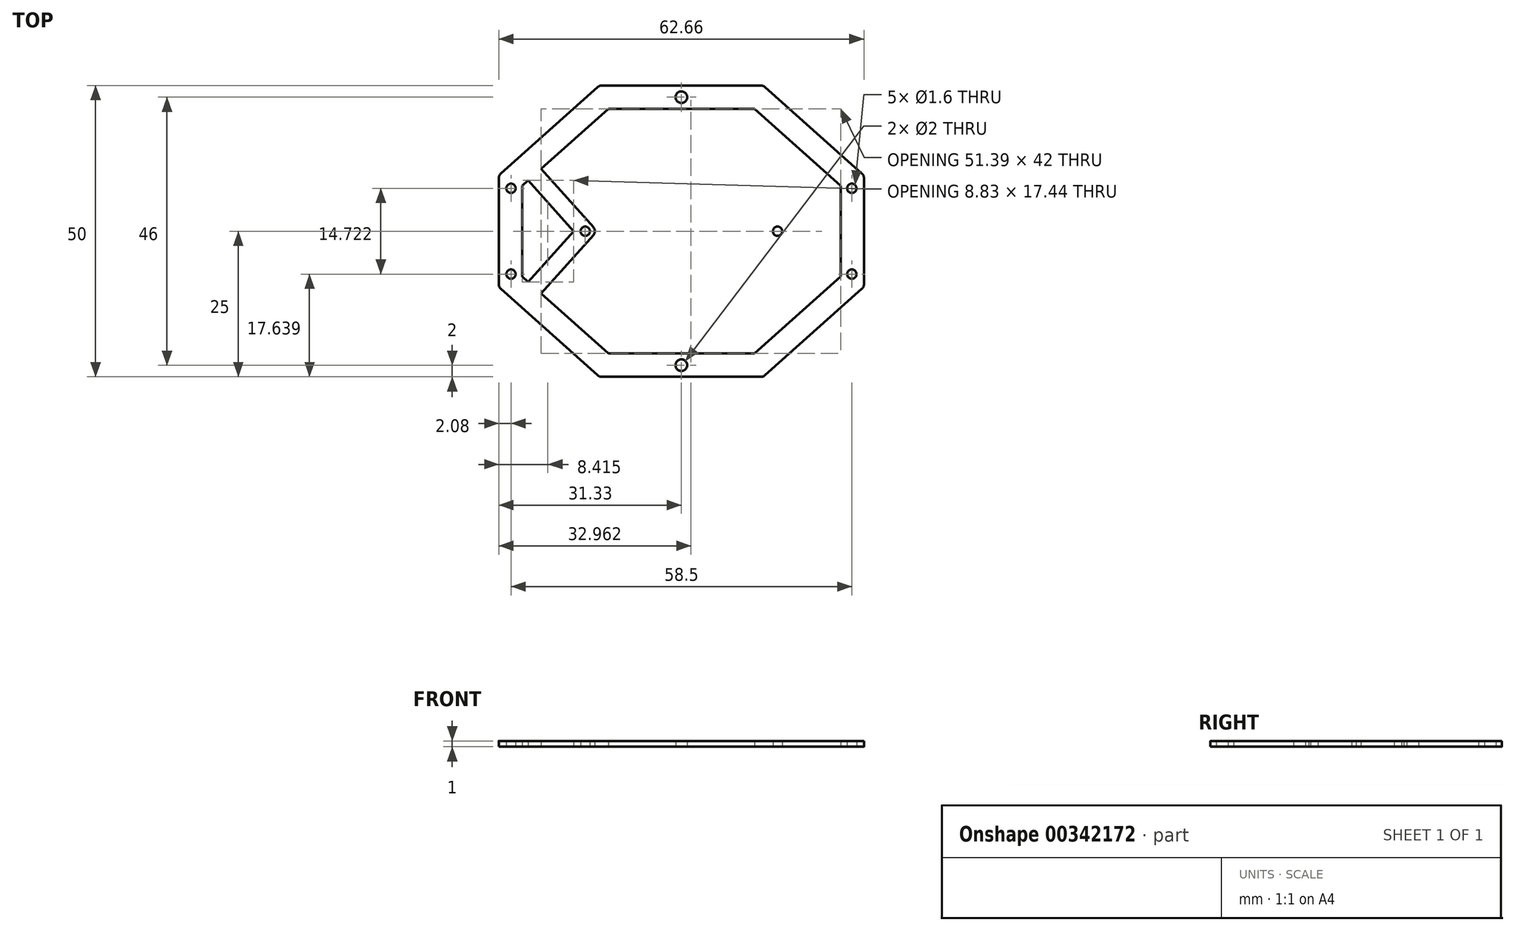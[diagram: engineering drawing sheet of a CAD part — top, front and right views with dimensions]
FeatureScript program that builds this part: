
annotation { "Feature Type Name" : "Feature", "Feature Type Description" : "" }
export const myFeature = defineFeature(function(context is Context, id is Id, definition is map)
    precondition{}
    {
        {
            var Q0;
            Q0=qCreatedBy(makeId("Top.planeOp"),FACE);
            var sketch = newSketch(context, id + "F0", { "sketchPlane" : qUnion([Q0])});
            skPoint(sketch, "E0", {"position": v(0, 25) * mm});
            skPoint(sketch, "E1", {"position": v(25, 0) * mm});
            skPoint(sketch, "E2", {"position": v(16.5, 0) * mm});
            skPoint(sketch, "E3.1.0", {"position": v(29.25, -7.36) * mm});
            skPoint(sketch, "E3.2.0", {"position": v(29.25, 7.36) * mm});
            skLineSegment(sketch, "E4", {"start": v(0, 25) * mm, "end": v(14.07, 25) * mm});
            skPoint(sketch, "E5.MirrorP", {"position": v(-29.25, 7.36) * mm});
            skPoint(sketch, "E6.MirrorP", {"position": v(-16.5, 0) * mm});
            skPoint(sketch, "E7.MirrorP", {"position": v(-25, 0) * mm});
            skPoint(sketch, "E8.MirrorP", {"position": v(-29.25, -7.36) * mm});
            skCircle(sketch, "E9", {"center": v(29.25, 7.36) * mm, "radius": 0.8 * mm});
            skCircle(sketch, "E10.1.0", {"center": v(16.5, 0) * mm, "radius": 0.8 * mm});
            skCircle(sketch, "E10.2.0", {"center": v(29.25, -7.36) * mm, "radius": 0.8 * mm});
            skLineSegment(sketch, "E11", {"start": v(31.33, 0) * mm, "end": v(31.33, 9.58) * mm});
            skLineSegment(sketch, "E12", {"start": v(14.07, 25) * mm, "end": v(31.33, 9.58) * mm});
            skLineSegment(sketch, "E13.0", {"start": v(27.33, -0.08) * mm, "end": v(27.33, 7.8) * mm});
            skLineSegment(sketch, "E13.1", {"start": v(12.54, 21) * mm, "end": v(27.33, 7.8) * mm});
            skLineSegment(sketch, "E13.2", {"start": v(0, 21) * mm, "end": v(12.54, 21) * mm});
            skPoint(sketch, "E14", {"position": v(18.5, 0) * mm});
            skLineSegment(sketch, "E15", {"start": v(18.5, 0) * mm, "end": v(28.95, 11.7) * mm});
            skPoint(sketch, "E16", {"position": v(26.29, 8.72) * mm});
            skPoint(sketch, "E17", {"position": v(14.5, 0) * mm});
            skLineSegment(sketch, "E18", {"start": v(14.5, 0) * mm, "end": v(26.73, 13.69) * mm});
            skPoint(sketch, "E19", {"position": v(24.06, 10.7) * mm});
            skPoint(sketch, "E20", {"position": v(26.73, 13.69) * mm});
            skPoint(sketch, "E21", {"position": v(28.95, 11.7) * mm});
            skCircle(sketch, "E22.MirrorC", {"center": v(-29.25, -7.36) * mm, "radius": 0.8 * mm});
            skCircle(sketch, "E23.MirrorC", {"center": v(-29.25, 7.36) * mm, "radius": 0.8 * mm});
            skCircle(sketch, "E24.MirrorC", {"center": v(-16.5, 0) * mm, "radius": 0.8 * mm});
            skPoint(sketch, "E25.MirrorP", {"position": v(-14.5, 0) * mm});
            skLineSegment(sketch, "E26.MirrorCS", {"start": v(-14.07, 25) * mm, "end": v(-31.33, 9.58) * mm});
            skLineSegment(sketch, "E27.MirrorCS", {"start": v(0, 21) * mm, "end": v(-12.54, 21) * mm});
            skLineSegment(sketch, "E28.MirrorCS", {"start": v(-18.5, 0) * mm, "end": v(-28.95, 11.7) * mm});
            skLineSegment(sketch, "E29.MirrorCS", {"start": v(-31.33, 0) * mm, "end": v(-31.33, 9.58) * mm});
            skPoint(sketch, "E30.MirrorP", {"position": v(-24.06, 10.7) * mm});
            skPoint(sketch, "E31.MirrorP", {"position": v(-26.73, 13.69) * mm});
            skPoint(sketch, "E32.MirrorP", {"position": v(-26.29, 8.72) * mm});
            skLineSegment(sketch, "E33.MirrorCS", {"start": v(-14.5, 0) * mm, "end": v(-26.73, 13.69) * mm});
            skLineSegment(sketch, "E34.MirrorCS", {"start": v(-12.54, 21) * mm, "end": v(-27.33, 7.8) * mm});
            skPoint(sketch, "E35.MirrorP", {"position": v(-18.5, 0) * mm});
            skPoint(sketch, "E36.MirrorP", {"position": v(-28.95, 11.7) * mm});
            skLineSegment(sketch, "E37.MirrorCS", {"start": v(0, 25) * mm, "end": v(-14.07, 25) * mm});
            skLineSegment(sketch, "E38.MirrorCS", {"start": v(-27.33, -0.08) * mm, "end": v(-27.33, 7.8) * mm});
            skPoint(sketch, "E39.MirrorP", {"position": v(0, -25) * mm});
            skLineSegment(sketch, "E40.MirrorCS", {"start": v(-14.5, 0) * mm, "end": v(-26.73, -13.69) * mm});
            skPoint(sketch, "E41.MirrorP", {"position": v(26.73, -13.69) * mm});
            skPoint(sketch, "E42.MirrorP", {"position": v(26.29, -8.72) * mm});
            skPoint(sketch, "E43.MirrorP", {"position": v(-26.29, -8.72) * mm});
            skLineSegment(sketch, "E44.MirrorCS", {"start": v(-31.33, 0) * mm, "end": v(-31.33, -9.58) * mm});
            skLineSegment(sketch, "E45.MirrorCS", {"start": v(-27.33, 0.08) * mm, "end": v(-27.33, -7.8) * mm});
            skPoint(sketch, "E46.MirrorP", {"position": v(24.06, -10.7) * mm});
            skPoint(sketch, "E47.MirrorP", {"position": v(-26.73, -13.69) * mm});
            skLineSegment(sketch, "E48.MirrorCS", {"start": v(-18.5, 0) * mm, "end": v(-28.95, -11.7) * mm});
            skLineSegment(sketch, "E49.MirrorCS", {"start": v(0, -25) * mm, "end": v(-14.07, -25) * mm});
            skLineSegment(sketch, "E50.MirrorCS", {"start": v(14.07, -25) * mm, "end": v(31.33, -9.58) * mm});
            skPoint(sketch, "E51.MirrorP", {"position": v(28.95, -11.7) * mm});
            skLineSegment(sketch, "E52.MirrorCS", {"start": v(31.33, 0) * mm, "end": v(31.33, -9.58) * mm});
            skLineSegment(sketch, "E53.MirrorCS", {"start": v(18.5, 0) * mm, "end": v(28.95, -11.7) * mm});
            skLineSegment(sketch, "E54.MirrorCS", {"start": v(-14.07, -25) * mm, "end": v(-31.33, -9.58) * mm});
            skLineSegment(sketch, "E55.MirrorCS", {"start": v(-12.54, -21) * mm, "end": v(-27.33, -7.8) * mm});
            skLineSegment(sketch, "E56.MirrorCS", {"start": v(14.5, 0) * mm, "end": v(26.73, -13.69) * mm});
            skPoint(sketch, "E57.MirrorP", {"position": v(-24.06, -10.7) * mm});
            skLineSegment(sketch, "E58.MirrorCS", {"start": v(0, -25) * mm, "end": v(14.07, -25) * mm});
            skLineSegment(sketch, "E59.MirrorCS", {"start": v(0, -21) * mm, "end": v(-12.54, -21) * mm});
            skLineSegment(sketch, "E60.MirrorCS", {"start": v(0, -21) * mm, "end": v(12.54, -21) * mm});
            skLineSegment(sketch, "E61.MirrorCS", {"start": v(12.54, -21) * mm, "end": v(27.33, -7.8) * mm});
            skLineSegment(sketch, "E62.MirrorCS", {"start": v(27.33, 0.08) * mm, "end": v(27.33, -7.8) * mm});
            skPoint(sketch, "E63.MirrorP", {"position": v(-28.95, -11.7) * mm});
            skPoint(sketch, "E64", {"position": v(0, 23) * mm});
            skCircle(sketch, "E65", {"center": v(0, 23) * mm, "radius": 1 * mm});
            skCircle(sketch, "E66.MirrorC", {"center": v(0, -23) * mm, "radius": 1 * mm});
            skSolve(sketch);
        }
        {
            var Q0;
            {var subQ6=sQuery(id+"F0.wireOp",EDGE,"E4");Q0=makeQuery(id+"F0.imprint","IMPRINT",FACE,{"disambiguationData":[TD([[makeQuery(id+"F0.imprint","IMPRINT",EDGE,{"derivedFrom":subQ6}),-1.0]])]});}
            var Q1;
            {var subQ0=sQuery(id+"F0.wireOp",EDGE,"E28.MirrorCS");var subQ1=sQuery(id+"F0.wireOp",EDGE,"E26.MirrorCS");var subQ2=makeQuery(id+"F0.imprint","INTERSECT",VERTEX,{"derivedFrom":[subQ1,subQ0]});Q1=makeQuery(id+"F0.imprint","IMPRINT",FACE,{"disambiguationData":[TD([[makeQuery(id+"F0.imprint","IMPRINT",EDGE,{"disambiguationData":[TD([[subQ2,1.0]])],"derivedFrom":subQ1}),1.0]])]});}
            var Q2;
            {var subQ9=sQuery(id+"F0.wireOp",EDGE,"E29.MirrorCS");Q2=makeQuery(id+"F0.imprint","IMPRINT",FACE,{"disambiguationData":[TD([[makeQuery(id+"F0.imprint","IMPRINT",EDGE,{"derivedFrom":subQ9}),-1.0]])]});}
            var Q3;
            Q3=makeQuery(id+"F0.imprint","IMPRINT",FACE,{"disambiguationData":[TD([[makeQuery(id+"F0.imprint","IMPRINT",EDGE,{"derivedFrom":sQuery(id+"F0.wireOp",EDGE,"E24.MirrorC")}),-1.0]])]});
            var Q4;
            {var subQ0=sQuery(id+"F0.wireOp",EDGE,"E54.MirrorCS");var subQ1=sQuery(id+"F0.wireOp",EDGE,"E40.MirrorCS");var subQ2=makeQuery(id+"F0.imprint","INTERSECT",VERTEX,{"derivedFrom":[subQ1,subQ0]});Q4=makeQuery(id+"F0.imprint","IMPRINT",FACE,{"disambiguationData":[TD([[makeQuery(id+"F0.imprint","IMPRINT",EDGE,{"disambiguationData":[TD([[subQ2,1.0]])],"derivedFrom":subQ1}),-1.0]])]});}
            var Q5;
            {var subQ3=sQuery(id+"F0.wireOp",EDGE,"E49.MirrorCS");Q5=makeQuery(id+"F0.imprint","IMPRINT",FACE,{"disambiguationData":[TD([[makeQuery(id+"F0.imprint","IMPRINT",EDGE,{"derivedFrom":subQ3}),-1.0]])]});}
            var Q6;
            Q6=makeQuery(id+"F0.imprint","IMPRINT",FACE,{"disambiguationData":[TD([[makeQuery(id+"F0.imprint","IMPRINT",EDGE,{"derivedFrom":sQuery(id+"F0.wireOp",EDGE,"E10.1.0")}),1.0]])]});
            var Q7;
            {var subQ5=sQuery(id+"F0.wireOp",EDGE,"E11");Q7=makeQuery(id+"F0.imprint","IMPRINT",FACE,{"disambiguationData":[TD([[makeQuery(id+"F0.imprint","IMPRINT",EDGE,{"derivedFrom":subQ5}),1.0]])]});}
            var Q8;
            {var subQ0=sQuery(id+"F0.wireOp",EDGE,"E15");var subQ1=sQuery(id+"F0.wireOp",EDGE,"E12");var subQ2=makeQuery(id+"F0.imprint","INTERSECT",VERTEX,{"derivedFrom":[subQ1,subQ0]});Q8=makeQuery(id+"F0.imprint","IMPRINT",FACE,{"disambiguationData":[TD([[makeQuery(id+"F0.imprint","IMPRINT",EDGE,{"disambiguationData":[TD([[subQ2,1.0]])],"derivedFrom":subQ1}),-1.0]])]});}
            var Q9;
            {var subQ0=sQuery(id+"F0.wireOp",EDGE,"E53.MirrorCS");var subQ1=sQuery(id+"F0.wireOp",EDGE,"E50.MirrorCS");var subQ2=makeQuery(id+"F0.imprint","INTERSECT",VERTEX,{"derivedFrom":[subQ1,subQ0]});Q9=makeQuery(id+"F0.imprint","IMPRINT",FACE,{"disambiguationData":[TD([[makeQuery(id+"F0.imprint","IMPRINT",EDGE,{"disambiguationData":[TD([[subQ2,1.0]])],"derivedFrom":subQ1}),1.0]])]});}
            extrude(context, id + "F1", {"entities" : qUnion([Q0, Q1, Q2, Q3, Q4, Q5, Q6, Q7, Q8, Q9]), "depth" : 1 * mm});
        }
        {
            var Q0;
            Q0=makeQuery(id+"F1.opExtrude","SWEPT_EDGE",EDGE,{"disambiguationData":[OSD([sQuery(id+"F0.wireOp",EDGE,"E26.MirrorCS"),sQuery(id+"F0.wireOp",EDGE,"E37.MirrorCS")])]});
            var Q1;
            Q1=makeQuery(id+"F1.opExtrude","SWEPT_EDGE",EDGE,{"disambiguationData":[OSD([sQuery(id+"F0.wireOp",EDGE,"E26.MirrorCS"),sQuery(id+"F0.wireOp",EDGE,"E29.MirrorCS")])]});
            var Q2;
            Q2=makeQuery(id+"F1.opExtrude","SWEPT_EDGE",EDGE,{"disambiguationData":[OSD([sQuery(id+"F0.wireOp",EDGE,"E44.MirrorCS"),sQuery(id+"F0.wireOp",EDGE,"E54.MirrorCS")])]});
            var Q3;
            Q3=makeQuery(id+"F1.opExtrude","SWEPT_EDGE",EDGE,{"disambiguationData":[OSD([sQuery(id+"F0.wireOp",EDGE,"E49.MirrorCS"),sQuery(id+"F0.wireOp",EDGE,"E54.MirrorCS")])]});
            var Q4;
            Q4=makeQuery(id+"F1.opExtrude","SWEPT_EDGE",EDGE,{"disambiguationData":[OSD([sQuery(id+"F0.wireOp",EDGE,"E50.MirrorCS"),sQuery(id+"F0.wireOp",EDGE,"E58.MirrorCS")])]});
            var Q5;
            Q5=makeQuery(id+"F1.opExtrude","SWEPT_EDGE",EDGE,{"disambiguationData":[OSD([sQuery(id+"F0.wireOp",EDGE,"E50.MirrorCS"),sQuery(id+"F0.wireOp",EDGE,"E52.MirrorCS")])]});
            var Q6;
            Q6=makeQuery(id+"F1.opExtrude","SWEPT_EDGE",EDGE,{"disambiguationData":[OSD([sQuery(id+"F0.wireOp",EDGE,"E11"),sQuery(id+"F0.wireOp",EDGE,"E12")])]});
            var Q7;
            Q7=makeQuery(id+"F1.opExtrude","SWEPT_EDGE",EDGE,{"disambiguationData":[OSD([sQuery(id+"F0.wireOp",EDGE,"E4"),sQuery(id+"F0.wireOp",EDGE,"E12")])]});
            var Q8;
            Q8=makeQuery(id+"F1.opExtrude","SWEPT_EDGE",EDGE,{"disambiguationData":[OSD([sQuery(id+"F0.wireOp",EDGE,"E18"),sQuery(id+"F0.wireOp",EDGE,"E56.MirrorCS")])]});
            var Q9;
            Q9=makeQuery(id+"F1.opExtrude","SWEPT_EDGE",EDGE,{"disambiguationData":[OSD([sQuery(id+"F0.wireOp",EDGE,"E33.MirrorCS"),sQuery(id+"F0.wireOp",EDGE,"E40.MirrorCS")])]});
            fillet(context, id + "F2", {"entities" : qUnion([Q0, Q1, Q2, Q3, Q4, Q5, Q6, Q7, Q8, Q9]), "radius" : 1 * mm, "tangentPropagation" : true, "allowEdgeOverflow" : false});
        }
    });
